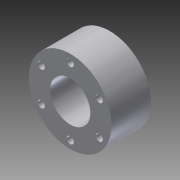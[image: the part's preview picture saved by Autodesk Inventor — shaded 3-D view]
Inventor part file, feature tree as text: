
AUTODESK INVENTOR PART (.ipt)
format: ipt  version: 2014 SP1 (Build 180222100, 222)  size: 210,944 bytes
history: native  units: in
note: dims shown in document units (in); Inventor stores cm internally (conversion verified against a paired STEP export)
features: extrude x1, sketch x1
ambient origin geometry x8: Origin, YZ Plane, XZ Plane, XY Plane, X Axis, Y Axis, Z Axis, Center Point
bodies: Solid1 (feature_tree)
feature tree (2):
  extrude  "Extrusion1"  [1 undecoded]
  sketch  "Sketch1"  dims[d0=1.106in d1=0.0in]
note: 1 required parameter value undecoded (feature->parameter linkage not recoverable at this tier; creation-order binding heuristic only, values carry confidence <= 0.55)
